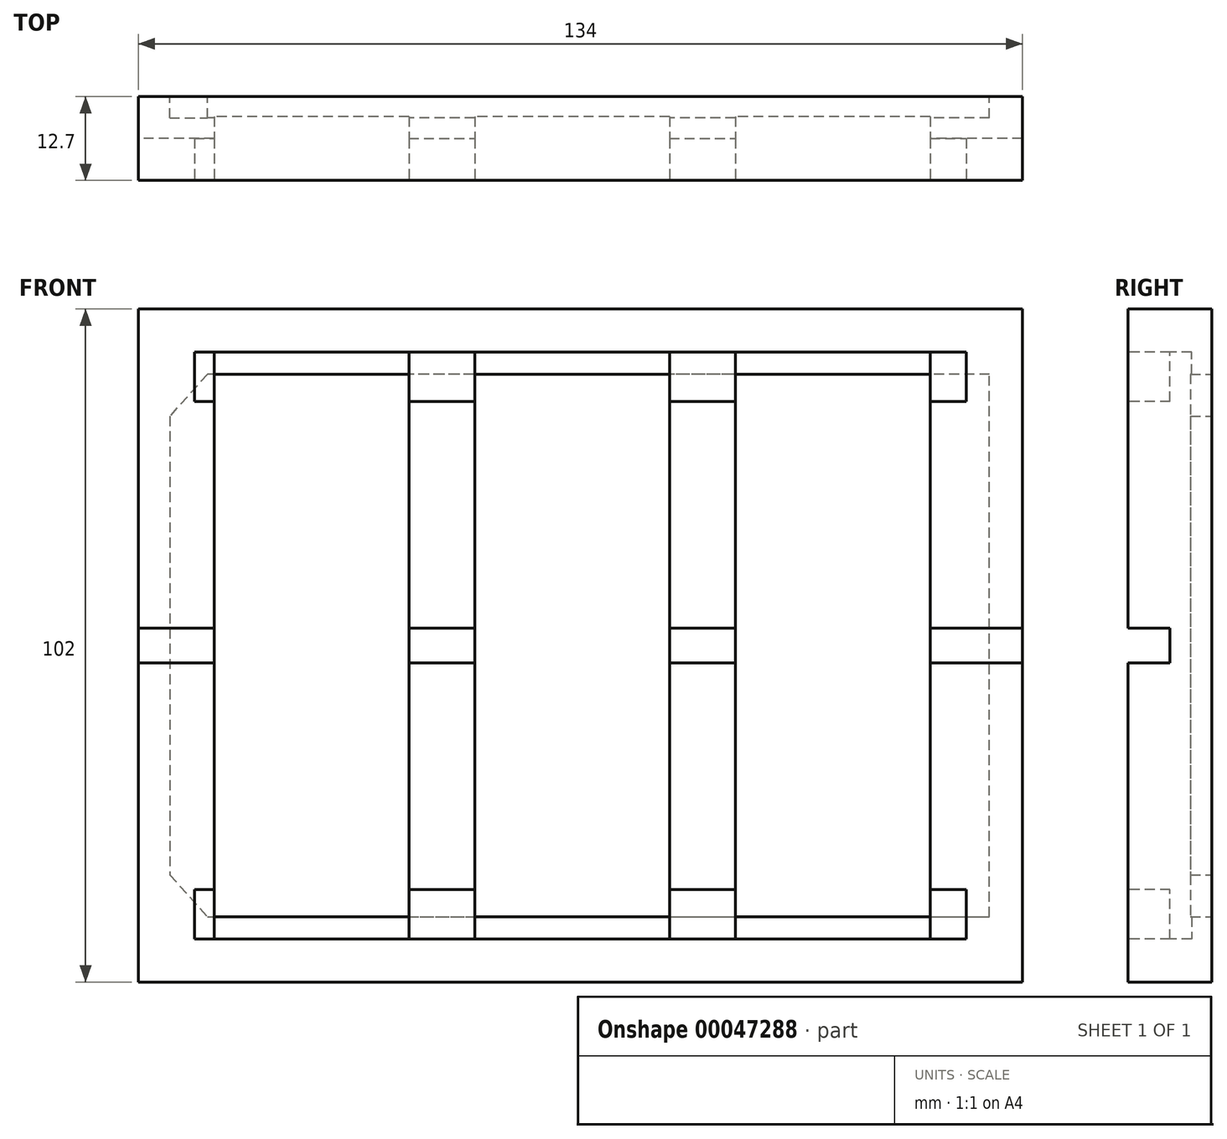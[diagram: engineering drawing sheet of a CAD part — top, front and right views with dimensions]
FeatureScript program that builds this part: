
annotation { "Feature Type Name" : "Feature", "Feature Type Description" : "" }
export const myFeature = defineFeature(function(context is Context, id is Id, definition is map)
    precondition{}
    {
        {
            var Q0;
            Q0=qCreatedBy(makeId("Front.planeOp"),FACE);
            var sketch = newSketch(context, id + "F0", { "sketchPlane" : qUnion([Q0])});
            skLineSegment(sketch, "E0.rect.bottom", {"start": v(67, -51) * mm, "end": v(-67, -51) * mm});
            skLineSegment(sketch, "E0.rect.top", {"start": v(67, 51) * mm, "end": v(-67, 51) * mm});
            skLineSegment(sketch, "E0.rect.left", {"start": v(67, -51) * mm, "end": v(67, 51) * mm});
            skLineSegment(sketch, "E0.rect.right", {"start": v(-67, -51) * mm, "end": v(-67, 51) * mm});
            skPoint(sketch, "E0.rect.middle", {"position": v(0, 0) * mm});
            skLineSegment(sketch, "E1", {"start": v(0, 51) * mm, "end": v(0, -51) * mm, "construction": true});
            skLineSegment(sketch, "E2", {"start": v(-67, 0) * mm, "end": v(67, 0) * mm, "construction": true});
            skSolve(sketch);
        }
        {
            var Q0;
            Q0=makeQuery(id+"F0.imprint","IMPRINT",FACE,{"disambiguationData":[TD([[makeQuery(id+"F0.imprint","IMPRINT",EDGE,{"derivedFrom":sQuery(id+"F0.wireOp",EDGE,"E0.rect.bottom")}),-1.0]])]});
            extrude(context, id + "F1", {"entities" : qUnion([Q0]), "depth" : 12.7 * mm});
        }
        {
            var Q0;
            Q0=makeQuery(id+"F1.opExtrude","CAP_FACE",FACE,{"disambiguationData":[OSD([sQuery(id+"F0.wireOp",EDGE,"E0.rect.bottom"),sQuery(id+"F0.wireOp",EDGE,"E0.rect.top"),sQuery(id+"F0.wireOp",EDGE,"E0.rect.left"),sQuery(id+"F0.wireOp",EDGE,"E0.rect.right")])],"isStart":false});
            var sketch = newSketch(context, id + "F2", { "sketchPlane" : qUnion([Q0])});
            skLineSegment(sketch, "E3.bottom", {"start": v(-16, 39.8) * mm, "end": v(13.5, 39.8) * mm});
            skLineSegment(sketch, "E3.top", {"start": v(-16, -39.8) * mm, "end": v(13.5, -39.8) * mm});
            skLineSegment(sketch, "E3.left", {"start": v(-16, 39.8) * mm, "end": v(-16, -39.8) * mm});
            skLineSegment(sketch, "E3.right", {"start": v(13.5, 39.8) * mm, "end": v(13.5, -39.8) * mm});
            skLineSegment(sketch, "E4.bottom", {"start": v(23.5, 39.8) * mm, "end": v(53, 39.8) * mm});
            skLineSegment(sketch, "E4.top", {"start": v(23.5, -39.8) * mm, "end": v(53, -39.8) * mm});
            skLineSegment(sketch, "E4.left", {"start": v(23.5, 39.8) * mm, "end": v(23.5, -39.8) * mm});
            skLineSegment(sketch, "E4.right", {"start": v(53, 39.8) * mm, "end": v(53, -39.8) * mm});
            skLineSegment(sketch, "E5.bottom", {"start": v(-55.5, 39.8) * mm, "end": v(-26, 39.8) * mm});
            skLineSegment(sketch, "E5.top", {"start": v(-55.5, -39.8) * mm, "end": v(-26, -39.8) * mm});
            skLineSegment(sketch, "E5.left", {"start": v(-55.5, 39.8) * mm, "end": v(-55.5, -39.8) * mm});
            skLineSegment(sketch, "E5.right", {"start": v(-26, 39.8) * mm, "end": v(-26, -39.8) * mm});
            skLineSegment(sketch, "E6", {"start": v(-67, 0) * mm, "end": v(-55.5, 0) * mm, "construction": true});
            skLineSegment(sketch, "E7", {"start": v(53, -16.02) * mm, "end": v(67, -16.02) * mm});
            skSolve(sketch);
        }
        {
            var Q0;
            Q0=qSketchRegion(id+"F2",true);
            extrude(context, id + "F3", {"entities" : qUnion([Q0]), "operationType" : NewBodyOperationType.REMOVE, "oppositeDirection" : true, "depth" : 12.7 * mm});
        }
        {
            var Q0;
            Q0=makeQuery(id+"F1.opExtrude","CAP_FACE",FACE,{"disambiguationData":[OSD([sQuery(id+"F0.wireOp",EDGE,"E0.rect.bottom"),sQuery(id+"F0.wireOp",EDGE,"E0.rect.top"),sQuery(id+"F0.wireOp",EDGE,"E0.rect.left"),sQuery(id+"F0.wireOp",EDGE,"E0.rect.right")])],"isStart":false});
            var sketch = newSketch(context, id + "F4", { "sketchPlane" : qUnion([Q0])});
            skLineSegment(sketch, "E8.bottom", {"start": v(-58.5, 44.5) * mm, "end": v(58.5, 44.5) * mm});
            skLineSegment(sketch, "E8.top", {"start": v(-58.5, 37) * mm, "end": v(58.5, 37) * mm});
            skLineSegment(sketch, "E8.left", {"start": v(-58.5, 44.5) * mm, "end": v(-58.5, 37) * mm});
            skLineSegment(sketch, "E8.right", {"start": v(58.5, 44.5) * mm, "end": v(58.5, 37) * mm});
            skPoint(sketch, "E9.rect.middle", {"position": v(0, 0) * mm});
            skLineSegment(sketch, "E10.rect.bottom", {"start": v(67, -2.63) * mm, "end": v(-67, -2.63) * mm});
            skLineSegment(sketch, "E10.rect.top", {"start": v(67, 2.62) * mm, "end": v(-67, 2.62) * mm});
            skLineSegment(sketch, "E10.rect.left", {"start": v(67, -2.63) * mm, "end": v(67, 2.62) * mm});
            skLineSegment(sketch, "E10.rect.right", {"start": v(-67, -2.63) * mm, "end": v(-67, 2.62) * mm});
            skPoint(sketch, "E11", {"position": v(-67, 0) * mm});
            skPoint(sketch, "E12", {"position": v(67, 0) * mm});
            skLineSegment(sketch, "E13", {"start": v(-67, 0) * mm, "end": v(67, 0) * mm, "construction": true});
            skLineSegment(sketch, "E14.MirrorCS", {"start": v(-58.5, -44.5) * mm, "end": v(-58.5, -37) * mm});
            skLineSegment(sketch, "E15.MirrorCS", {"start": v(-58.5, -44.5) * mm, "end": v(58.5, -44.5) * mm});
            skLineSegment(sketch, "E16.MirrorCS", {"start": v(58.5, -44.5) * mm, "end": v(58.5, -37) * mm});
            skLineSegment(sketch, "E17.MirrorCS", {"start": v(-58.5, -37) * mm, "end": v(58.5, -37) * mm});
            skLineSegment(sketch, "E18", {"start": v(-58.5, 37) * mm, "end": v(-67, 37) * mm});
            skLineSegment(sketch, "E19", {"start": v(58.5, 37) * mm, "end": v(67, 37) * mm});
            skSolve(sketch);
        }
        {
            var Q0;
            Q0=qSketchRegion(id+"F4",true);
            extrude(context, id + "F5", {"entities" : qUnion([Q0]), "operationType" : NewBodyOperationType.REMOVE, "oppositeDirection" : true, "depth" : 6.35 * mm});
        }
        {
            var Q0;
            Q0=makeQuery(id+"F1.opExtrude","CAP_FACE",FACE,{"disambiguationData":[OSD([sQuery(id+"F0.wireOp",EDGE,"E0.rect.bottom"),sQuery(id+"F0.wireOp",EDGE,"E0.rect.top"),sQuery(id+"F0.wireOp",EDGE,"E0.rect.left"),sQuery(id+"F0.wireOp",EDGE,"E0.rect.right")])],"isStart":true});
            var sketch = newSketch(context, id + "F6", { "sketchPlane" : qUnion([Q0])});
            skPoint(sketch, "E20.rect.middle", {"position": v(0, 0) * mm});
            skSolve(sketch);
        }
        {
            var Q0;
            Q0=makeQuery(id+"F6.imprint","IMPRINT",FACE,{"disambiguationData":[TD([[makeQuery(id+"F6.imprint","IMPRINT",EDGE,{"derivedFrom":makeQuery(id+"F1.opExtrude","CAP_EDGE",EDGE,{"disambiguationData":[OSD([sQuery(id+"F0.wireOp",EDGE,"E0.rect.bottom")])],"isStart":true})}),1.0]])]});
            var sketch = newSketch(context, id + "F7", { "sketchPlane" : qUnion([Q0])});
            skLineSegment(sketch, "E21", {"start": v(-62, 41.12) * mm, "end": v(56.5, 41.12) * mm});
            skLineSegment(sketch, "E22", {"start": v(56.5, 41.12) * mm, "end": v(62.25, 34.75) * mm});
            skLineSegment(sketch, "E23", {"start": v(62.25, 34.75) * mm, "end": v(62.25, -34.75) * mm});
            skLineSegment(sketch, "E24", {"start": v(62.25, -34.75) * mm, "end": v(56.5, -41.12) * mm});
            skLineSegment(sketch, "E25", {"start": v(56.5, -41.12) * mm, "end": v(-62, -41.12) * mm});
            skLineSegment(sketch, "E26", {"start": v(-62, -41.12) * mm, "end": v(-62, 41.12) * mm});
            skPoint(sketch, "E27", {"position": v(62.25, 0) * mm});
            skPoint(sketch, "E28", {"position": v(-62, 0) * mm});
            skLineSegment(sketch, "E29.0", {"start": v(-67, 51) * mm, "end": v(67, 51) * mm, "construction": true});
            skLineSegment(sketch, "E30.0", {"start": v(-67, -51) * mm, "end": v(67, -51) * mm, "construction": true});
            skLineSegment(sketch, "E31", {"start": v(2.17, 51) * mm, "end": v(2.17, 41.12) * mm, "construction": true});
            skLineSegment(sketch, "E32", {"start": v(2.69, -41.12) * mm, "end": v(2.69, -51) * mm, "construction": true});
            skSolve(sketch);
        }
        {
            var Q0;
            Q0=qSketchRegion(id+"F7",true);
            extrude(context, id + "F8", {"entities" : qUnion([Q0]), "operationType" : NewBodyOperationType.REMOVE, "oppositeDirection" : true, "depth" : 3.25 * mm});
        }
        {
            var Q0;
            Q0=makeQuery(id+"F5.boolean.opBoolean","COPY",FACE,{"derivedFrom":makeQuery(id+"F5.opExtrude","CAP_FACE",FACE,{"disambiguationData":[OSD([sQuery(id+"F4.wireOp",EDGE,"E8.bottom"),sQuery(id+"F4.wireOp",EDGE,"E8.top"),sQuery(id+"F4.wireOp",EDGE,"E8.left"),sQuery(id+"F4.wireOp",EDGE,"E8.right")])],"isStart":false})});
            var sketch = newSketch(context, id + "F9", { "sketchPlane" : qUnion([Q0])});
            skLineSegment(sketch, "E33.bottom", {"start": v(-16, 39.8) * mm, "end": v(13.5, 39.8) * mm});
            skLineSegment(sketch, "E33.top", {"start": v(-16, 44.5) * mm, "end": v(13.5, 44.5) * mm});
            skLineSegment(sketch, "E33.left", {"start": v(-16, 39.8) * mm, "end": v(-16, 44.5) * mm});
            skLineSegment(sketch, "E33.right", {"start": v(13.5, 39.8) * mm, "end": v(13.5, 44.5) * mm});
            skLineSegment(sketch, "E34.bottom", {"start": v(23.5, 39.8) * mm, "end": v(53, 39.8) * mm});
            skLineSegment(sketch, "E34.top", {"start": v(23.5, 44.5) * mm, "end": v(53, 44.5) * mm});
            skLineSegment(sketch, "E34.left", {"start": v(23.5, 39.8) * mm, "end": v(23.5, 44.5) * mm});
            skLineSegment(sketch, "E34.right", {"start": v(53, 39.8) * mm, "end": v(53, 44.5) * mm});
            skLineSegment(sketch, "E35.bottom", {"start": v(-55.5, 39.8) * mm, "end": v(-26, 39.8) * mm});
            skLineSegment(sketch, "E35.top", {"start": v(-55.5, 44.5) * mm, "end": v(-26, 44.5) * mm});
            skLineSegment(sketch, "E35.left", {"start": v(-55.5, 39.8) * mm, "end": v(-55.5, 44.5) * mm});
            skLineSegment(sketch, "E35.right", {"start": v(-26, 39.8) * mm, "end": v(-26, 44.5) * mm});
            skPoint(sketch, "E36", {"position": v(-66.9, 0) * mm});
            skPoint(sketch, "E37", {"position": v(66.96, 0) * mm});
            skLineSegment(sketch, "E38", {"start": v(-66.9, 0) * mm, "end": v(66.96, 0) * mm, "construction": true});
            skLineSegment(sketch, "E39.MirrorCS", {"start": v(-55.5, -44.5) * mm, "end": v(-26, -44.5) * mm});
            skLineSegment(sketch, "E40.MirrorCS", {"start": v(-55.5, -39.8) * mm, "end": v(-55.5, -44.5) * mm});
            skLineSegment(sketch, "E41.MirrorCS", {"start": v(-55.5, -39.8) * mm, "end": v(-26, -39.8) * mm});
            skLineSegment(sketch, "E42.MirrorCS", {"start": v(-26, -39.8) * mm, "end": v(-26, -44.5) * mm});
            skLineSegment(sketch, "E43.MirrorCS", {"start": v(-16, -44.5) * mm, "end": v(13.5, -44.5) * mm});
            skLineSegment(sketch, "E44.MirrorCS", {"start": v(-16, -39.8) * mm, "end": v(-16, -44.5) * mm});
            skLineSegment(sketch, "E45.MirrorCS", {"start": v(13.5, -39.8) * mm, "end": v(13.5, -44.5) * mm});
            skLineSegment(sketch, "E46.MirrorCS", {"start": v(-16, -39.8) * mm, "end": v(13.5, -39.8) * mm});
            skLineSegment(sketch, "E47.MirrorCS", {"start": v(23.5, -44.5) * mm, "end": v(53, -44.5) * mm});
            skLineSegment(sketch, "E48.MirrorCS", {"start": v(23.5, -39.8) * mm, "end": v(23.5, -44.5) * mm});
            skLineSegment(sketch, "E49.MirrorCS", {"start": v(23.5, -39.8) * mm, "end": v(53, -39.8) * mm});
            skLineSegment(sketch, "E50.MirrorCS", {"start": v(53, -39.8) * mm, "end": v(53, -44.5) * mm});
            skSolve(sketch);
        }
        {
            var Q0;
            Q0=qSketchRegion(id+"F9",true);
            extrude(context, id + "F10", {"entities" : qUnion([Q0]), "operationType" : NewBodyOperationType.REMOVE, "oppositeDirection" : true, "depth" : 3.3 * mm});
        }
    });
